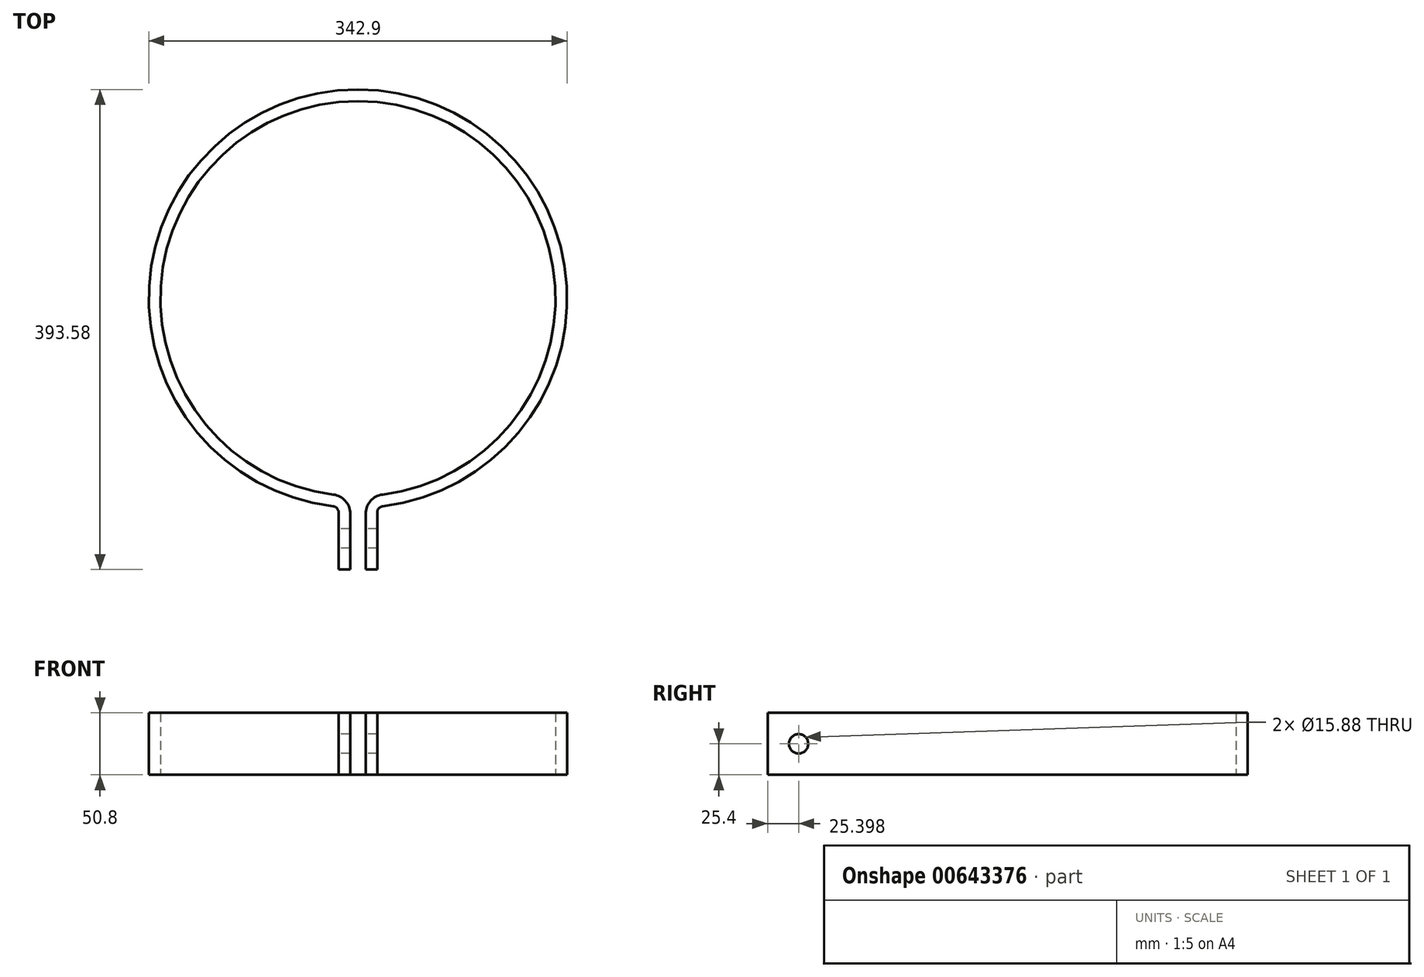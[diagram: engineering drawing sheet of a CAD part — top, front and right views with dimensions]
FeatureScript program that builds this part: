
annotation { "Feature Type Name" : "Feature", "Feature Type Description" : "" }
export const myFeature = defineFeature(function(context is Context, id is Id, definition is map)
    precondition{}
    {
        {
            var Q0;
            Q0=qCreatedBy(makeId("Top.planeOp"),FACE);
            var sketch = newSketch(context, id + "F0", { "sketchPlane" : qUnion([Q0])});
            skArc(sketch, "E0", {"start": v(6.35, -161.8) * mm, "mid": v(0, 161.93) * mm, "end": v(-6.35, -161.8) * mm});
            skArc(sketch, "E1", {"start": v(15.88, -170.71) * mm, "mid": v(0, 171.45) * mm, "end": v(-15.87, -170.71) * mm});
            skLineSegment(sketch, "E2", {"start": v(-6.35, -171.33) * mm, "end": v(-6.35, -222.13) * mm});
            skLineSegment(sketch, "E3", {"start": v(-6.35, -222.13) * mm, "end": v(-15.88, -222.13) * mm});
            skLineSegment(sketch, "E4", {"start": v(-15.88, -222.13) * mm, "end": v(-15.88, -170.71) * mm});
            skLineSegment(sketch, "E5.MirrorCS", {"start": v(6.35, -171.33) * mm, "end": v(6.35, -222.13) * mm});
            skLineSegment(sketch, "E6.MirrorCS", {"start": v(15.88, -222.13) * mm, "end": v(15.88, -170.71) * mm});
            skLineSegment(sketch, "E7.MirrorCS", {"start": v(6.35, -222.13) * mm, "end": v(15.88, -222.13) * mm});
            skLineSegment(sketch, "E8", {"start": v(6.35, -171.33) * mm, "end": v(6.35, -161.8) * mm});
            skLineSegment(sketch, "E9", {"start": v(-6.35, -171.33) * mm, "end": v(-6.35, -161.8) * mm});
            skSolve(sketch);
        }
        {
            var Q0;
            Q0 = qSketchRegion(id + "F0", true);
            extrude(context, id + "F1", {"entities" : qUnion([Q0]), "depth" : 50.8 * mm, "offsetDistance" : 25.4 * mm});
        }
        {
            var Q0;
            Q0=makeQuery(id+"F1.opExtrude","SWEPT_EDGE",EDGE,{"disambiguationData":[OSD([sQuery(id+"F0.wireOp",EDGE,"E1"),sQuery(id+"F0.wireOp",EDGE,"E4")])]});
            var Q1;
            Q1=makeQuery(id+"F1.opExtrude","SWEPT_EDGE",EDGE,{"disambiguationData":[OSD([sQuery(id+"F0.wireOp",EDGE,"E1"),sQuery(id+"F0.wireOp",EDGE,"E6.MirrorCS")])]});
            fillet(context, id + "F2", {"entities" : qUnion([Q0, Q1]), "radius" : 5.08 * mm, "tangentPropagation" : true, "allowEdgeOverflow" : false});
        }
        {
            var Q0;
            Q0=makeQuery(id+"F1.opExtrude","SWEPT_EDGE",EDGE,{"disambiguationData":[OSD([sQuery(id+"F0.wireOp",EDGE,"E0"),sQuery(id+"F0.wireOp",EDGE,"E9")])]});
            var Q1;
            Q1=makeQuery(id+"F1.opExtrude","SWEPT_EDGE",EDGE,{"disambiguationData":[OSD([sQuery(id+"F0.wireOp",EDGE,"E0"),sQuery(id+"F0.wireOp",EDGE,"E8")])]});
            fillet(context, id + "F3", {"entities" : qUnion([Q0, Q1]), "radius" : 15.88 * mm, "tangentPropagation" : true, "allowEdgeOverflow" : false});
        }
        {
            var Q0;
            Q0=makeQuery(id+"F1.opExtrude","SWEPT_FACE",FACE,{"disambiguationData":[OSD([sQuery(id+"F0.wireOp",EDGE,"E4")])]});
            var sketch = newSketch(context, id + "F4", { "sketchPlane" : qUnion([Q0])});
            skCircle(sketch, "E10", {"center": v(196.73, 25.4) * mm, "radius": 7.94 * mm});
            skPoint(sketch, "E10.centerSnap0", {"position": v(222.13, 25.4) * mm});
            skSolve(sketch);
        }
        {
            var Q0;
            Q0 = qSketchRegion(id + "F4", true);
            extrude(context, id + "F5", {"entities" : qUnion([Q0]), "operationType" : NewBodyOperationType.REMOVE, "endBound" : BoundingType.THROUGH_ALL, "oppositeDirection" : true, "depth" : 25.4 * mm, "offsetDistance" : 25.4 * mm});
        }
    });
